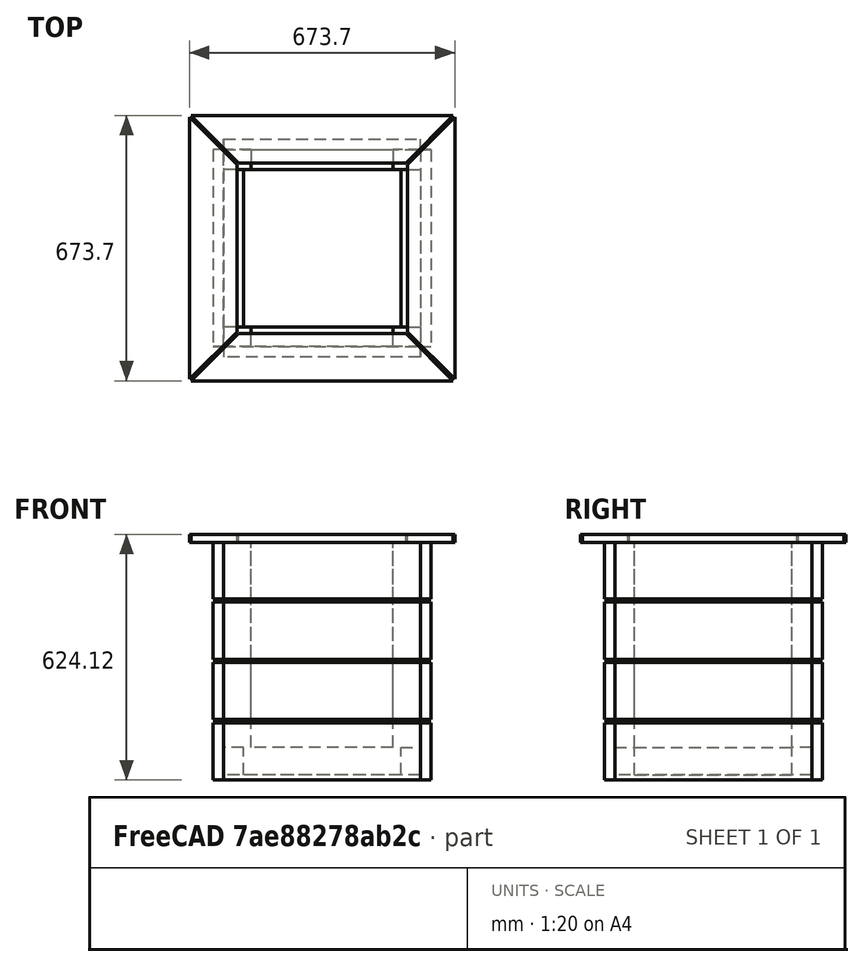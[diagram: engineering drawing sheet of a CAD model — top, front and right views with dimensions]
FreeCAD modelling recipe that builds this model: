
FCSTD DOCUMENT  (FreeCAD 0.18R16110 (Git))
Label: jardiniere
License: All rights reserved
LicenseURL: http://en.wikipedia.org/wiki/All_rights_reserved
objects: TechDraw::DrawViewDimension×11, TechDraw::DrawViewPart×6, Sketcher::SketchObject×4, PartDesign::Pad×4, PartDesign::Mirrored×4, TechDraw::DrawViewAnnotation×4, PartDesign::Plane×3, PartDesign::MultiTransform×3, PartDesign::PolarPattern×2, TechDraw::DrawViewSection×2, PartDesign::LinearPattern×1, PartDesign::Body×1, TechDraw::DrawSVGTemplate×1, TechDraw::DrawPage×1
note: 26 computed .brp shape members not serialized (recipe doc carries the construction recipe); baked Part::Feature solids carry a one-line shape summary decoded from their .brp

FEATURE [Sketcher::SketchObject] Sketch
  MapMode = 5
  Support = -> [XY_Plane]
  sketch-geometry (8):
    g0: LineSegment StartX=-250 StartY=250 StartZ=0 EndX=250 EndY=250 EndZ=0
    g1: LineSegment StartX=250 StartY=250 StartZ=0 EndX=250 EndY=-250 EndZ=0
    g2: LineSegment StartX=250 StartY=-250 StartZ=0 EndX=-250 EndY=-250 EndZ=0
    g3: LineSegment StartX=-250 StartY=-250 StartZ=0 EndX=-250 EndY=250 EndZ=0
    g4: LineSegment StartX=-200 StartY=200 StartZ=0 EndX=200 EndY=200 EndZ=0
    g5: LineSegment StartX=200 StartY=200 StartZ=0 EndX=200 EndY=-200 EndZ=0
    g6: LineSegment StartX=200 StartY=-200 StartZ=0 EndX=-200 EndY=-200 EndZ=0
    g7: LineSegment StartX=-200 StartY=-200 StartZ=0 EndX=-200 EndY=200 EndZ=0
  constraints (22):
    c: Coincident(g0,g1)
    c: Vertical(g1)
    c: Coincident(g1,g2)
    c: Horizontal(g2)
    c: Coincident(g2,g3)
    c: Coincident(g3,g0)
    c: DistanceX(g0,g0) = 500
    c: DistanceY(g3,g3) = 500
    c: Symmetric(g0,g2,g-1)
    c: Symmetric(g0,g0,g-2)
    c: Coincident(g4,g5)
    c: Coincident(g5,g6)
    c: Coincident(g6,g7)
    c: Coincident(g7,g4)
    c: Horizontal(g4)
    c: Horizontal(g6)
    c: Vertical(g5)
    c: Vertical(g7)
    c: DistanceX(g5,g1) = 50
    c: DistanceY(g1,g5) = 50
    c: DistanceY(g4,g0) = 50
    c: DistanceX(g0,g4) = 50
FEATURE [PartDesign::Pad] Pad
  Length = 70
  Length2 = 100
  Profile = -> Sketch
  Type = 0
FEATURE [PartDesign::Plane] DatumPlane
  Length = 808.439
  MapMode = 5
  Placement = pos=(0,0,70) rot=(0,0,1;0rad)
  ResizeMode = 0
  Support = -> [Pad]
  Width = 808.439
FEATURE [Sketcher::SketchObject] Sketch001
  ExternalGeometry = -> [Pad]
  MapMode = 5
  Placement = pos=(0,0,70) rot=(0,0,1;0rad)
  Support = -> [DatumPlane]
  sketch-geometry (4):
    g0: LineSegment StartX=-250 StartY=250 StartZ=0 EndX=-180 EndY=250 EndZ=0
    g1: LineSegment StartX=-180 StartY=250 StartZ=0 EndX=-180 EndY=200 EndZ=0
    g2: LineSegment StartX=-180 StartY=200 StartZ=0 EndX=-250 EndY=200 EndZ=0
    g3: LineSegment StartX=-250 StartY=200 StartZ=0 EndX=-250 EndY=250 EndZ=0
  constraints (11):
    c: Coincident(g0,g1)
    c: Coincident(g1,g2)
    c: Coincident(g2,g3)
    c: Coincident(g3,g0)
    c: Horizontal(g0)
    c: Horizontal(g2)
    c: Vertical(g1)
    c: Vertical(g3)
    c: Coincident(g0,g-4)
    c: PointOnObject(g1,g-6)
    c: DistanceX(g0,g0) = 70
FEATURE [PartDesign::Pad] Pad001
  BaseFeature = -> Pad
  Length = 520
  Length2 = 100
  Profile = -> Sketch001
  Type = 0
FEATURE [PartDesign::Mirrored] Mirrored
  MirrorPlane = -> Sketch001 [H_Axis]
FEATURE [PartDesign::Mirrored] Mirrored001
  MirrorPlane = -> Sketch001 [V_Axis]
FEATURE [PartDesign::MultiTransform] MultiTransform
  BaseFeature = -> Pad001
  Originals = -> [Pad001]
  Transformations = -> [Mirrored,Mirrored001]
FEATURE [PartDesign::Plane] DatumPlane001
  Length = 803.386
  MapMode = 5
  Placement = pos=(0,250,0) rot=(0,0.707107,0.707107;3.14159rad)
  ResizeMode = 0
  Support = -> [Pad001]
  Width = 753.809
FEATURE [Sketcher::SketchObject] Sketch002
  ExternalGeometry = -> [MultiTransform]
  MapMode = 5
  Placement = pos=(0,250,0) rot=(0,0.707107,0.707107;3.14159rad)
  Support = -> [DatumPlane001]
  sketch-geometry (4):
    g0: LineSegment StartX=-250 StartY=131.878 StartZ=0 EndX=250 EndY=131.878 EndZ=0
    g1: LineSegment StartX=250 StartY=131.878 StartZ=0 EndX=250 EndY=-13.1218 EndZ=0
    g2: LineSegment StartX=250 StartY=-13.1218 StartZ=0 EndX=-250 EndY=-13.1218 EndZ=0
    g3: LineSegment StartX=-250 StartY=-13.1218 StartZ=0 EndX=-250 EndY=131.878 EndZ=0
  constraints (11):
    c: Coincident(g0,g1)
    c: Coincident(g1,g2)
    c: Coincident(g2,g3)
    c: Coincident(g3,g0)
    c: Horizontal(g0)
    c: Horizontal(g2)
    c: Vertical(g1)
    c: Vertical(g3)
    c: PointOnObject(g1,g-4)
    c: DistanceY(g3,g3) = 145
    c: PointOnObject(g0,g-3)
FEATURE [PartDesign::Pad] Pad002
  BaseFeature = -> MultiTransform
  Length = 27
  Length2 = 100
  Profile = -> Sketch002
  Type = 0
FEATURE [PartDesign::LinearPattern] LinearPattern
  Direction = -> Sketch002 [V_Axis]
  Length = 460
  Occurrences = 4
FEATURE [PartDesign::Mirrored] Mirrored002
  MirrorPlane = -> XZ_Plane
FEATURE [PartDesign::PolarPattern] PolarPattern
  Angle = 90
  Axis = -> Z_Axis
  Occurrences = 2
FEATURE [PartDesign::MultiTransform] MultiTransform001
  BaseFeature = -> Pad002
  Originals = -> [Pad002]
  Transformations = -> [LinearPattern,Mirrored002,PolarPattern]
FEATURE [PartDesign::Plane] DatumPlane002
  Length = 808.439
  MapMode = 5
  Placement = pos=(0,0,590) rot=(0,0,1;0rad)
  ResizeMode = 0
  Support = -> [MultiTransform001]
  Width = 808.439
FEATURE [Sketcher::SketchObject] Sketch003
  MapMode = 5
  Placement = pos=(0,0,590) rot=(0,0,1;0rad)
  Support = -> [DatumPlane002]
  sketch-geometry (4):
    g0: LineSegment StartX=-332.5 StartY=336.85 StartZ=0 EndX=332.5 EndY=336.85 EndZ=0
    g1: LineSegment StartX=332.5 StartY=336.85 StartZ=0 EndX=212.5 EndY=216.85 EndZ=0
    g2: LineSegment StartX=212.5 StartY=216.85 StartZ=0 EndX=-212.5 EndY=216.85 EndZ=0
    g3: LineSegment StartX=-212.5 StartY=216.85 StartZ=0 EndX=-332.5 EndY=336.85 EndZ=0
  constraints (10):
    c: Coincident(g0,g1)
    c: Coincident(g1,g2)
    c: Coincident(g2,g3)
    c: Coincident(g3,g0)
    c: Angle(g3,g0) = 0.785398
    c: Angle(g0,g1) = 0.785398
    c: DistanceX(g2,g2) = 425
    c: DistanceY(g1,g0) = 120
    c: DistanceX(g0,g0) = 665
    c: Symmetric(g2,g1,g-2)
FEATURE [PartDesign::Pad] Pad003
  BaseFeature = -> MultiTransform001
  Length = 21
  Length2 = 100
  Profile = -> Sketch003
  Type = 0
FEATURE [PartDesign::Mirrored] Mirrored003
  MirrorPlane = -> Sketch003 [H_Axis]
FEATURE [PartDesign::PolarPattern] PolarPattern001
  Angle = 90
  Axis = -> Sketch003 [N_Axis]
  Occurrences = 2
FEATURE [PartDesign::MultiTransform] MultiTransform002
  BaseFeature = -> Pad003
  Originals = -> [Pad003]
  Transformations = -> [Mirrored003,PolarPattern001]
FEATURE [PartDesign::Body] Body
  Group = -> [Sketch,Pad,DatumPlane,Sketch001,Pad001,MultiTransform,Mirrored,Mirrored001,DatumPlane001,Sketch002,Pad002,MultiTransform001,LinearPattern,Mirrored002,PolarPattern,DatumPlane002,Sketch003,Pad003,MultiTransform002,Mirrored003,PolarPattern001]
  Origin = -> Origin
  Tip = -> MultiTransform002
FEATURE [TechDraw::DrawSVGTemplate] Template
  EditableTexts = Designed_by_Name=Y. Labrit; Drawing_number=Drawing number; FC-Date=01/07/2018; FC-SC=Scale; FC-SH=Sheet; FC-Title=Jardiniere cube; Subtitle=Subtitle; Weight=Weight
  Height = 210
  Orientation = 1
  Width = 297
FEATURE [TechDraw::DrawViewPart] View
  CoarseView = false
  Direction = (0,1,0)
  Focus = 100
  HardHidden = false
  IsoCount = 0
  IsoHidden = false
  IsoVisible = false
  LockPosition = false
  Perspective = false
  Rotation = 0
  Scale = 0.07
  ScaleType = 2
  SeamHidden = false
  SeamVisible = false
  SmoothHidden = false
  SmoothVisible = false
  Source = -> [MultiTransform002]
  X = 58.3303
  Y = 105.073
FEATURE [TechDraw::DrawViewSection] Section  label="Section A - A"
  BaseView = -> View
  CoarseView = false
  Direction = (0,0,1)
  Focus = 100
  FuseBeforeCut = true
  HardHidden = false
  HatchScale = 1
  IsoCount = 0
  IsoHidden = false
  IsoVisible = false
  LockPosition = false
  NameGeomPattern = Diamond
  Perspective = false
  Rotation = 0
  Scale = 0.07
  ScaleType = 2
  SeamHidden = false
  SeamVisible = false
  SectionDirection = 3
  SectionNormal = (0,0,1)
  SectionOrigin = (0,0,298.939)
  SectionSymbol = A
  SmoothHidden = false
  SmoothVisible = false
  Source = -> [MultiTransform002]
  X = 57.2775
  Y = 45.8237
FEATURE [TechDraw::DrawViewSection] Section001  label="Section A - A001"
  BaseView = -> View
  CoarseView = false
  Direction = (1,0,0)
  Focus = 100
  FuseBeforeCut = true
  HardHidden = false
  HatchScale = 1
  IsoCount = 0
  IsoHidden = false
  IsoVisible = false
  LockPosition = false
  NameGeomPattern = Diamond
  Perspective = false
  Rotation = 0
  Scale = 0.07
  ScaleType = 2
  SeamHidden = false
  SeamVisible = false
  SectionDirection = 0
  SectionNormal = (1,0,0)
  SectionOrigin = (0,0,298.94)
  SectionSymbol = A
  SmoothHidden = false
  SmoothVisible = false
  Source = -> [MultiTransform002]
  X = 120.156
  Y = 104.575
FEATURE [TechDraw::DrawViewPart] View001
  CoarseView = false
  Direction = (0,0,1)
  Focus = 100
  HardHidden = false
  IsoCount = 0
  IsoHidden = false
  IsoVisible = false
  LockPosition = false
  Perspective = false
  Rotation = 0
  Scale = 0.05
  ScaleType = 2
  SeamHidden = false
  SeamVisible = false
  SmoothHidden = false
  SmoothVisible = false
  Source = -> [MultiTransform002]
  X = 57.2911
  Y = 163.823
FEATURE [TechDraw::DrawViewDimension] Dimension014
  Arbitrary = false
  FormatSpec = %.2f
  LockPosition = false
  MeasureType = 1
  OverTolerance = 0
  References2D = -> [Section]
  Rotation = 0
  ScaleType = 0
  Type = 2
  UnderTolerance = 0
  X = 28.896
  Y = -1.49114
FEATURE [TechDraw::DrawViewDimension] Dimension015
  Arbitrary = false
  FormatSpec = %.2f
  LockPosition = false
  MeasureType = 1
  OverTolerance = 0
  References2D = -> [Section]
  Rotation = 0
  ScaleType = 0
  Type = 1
  UnderTolerance = 0
  X = 0
  Y = -27.0321
FEATURE [TechDraw::DrawViewDimension] Dimension016
  Arbitrary = false
  FormatSpec = %.2f
  LockPosition = false
  MeasureType = 1
  OverTolerance = 0
  References2D = -> [Section001]
  Rotation = 0
  ScaleType = 0
  Type = 2
  UnderTolerance = 0
  X = 27.7953
  Y = -6.48469
FEATURE [TechDraw::DrawViewDimension] Dimension017
  Arbitrary = false
  FormatSpec = %.2f
  LockPosition = false
  MeasureType = 1
  OverTolerance = 0
  References2D = -> [Section001]
  Rotation = 0
  ScaleType = 0
  Type = 1
  UnderTolerance = 0
  X = 35.1592
  Y = -28.482
FEATURE [TechDraw::DrawViewDimension] Dimension018
  Arbitrary = false
  FormatSpec = %.2f
  LockPosition = false
  MeasureType = 1
  OverTolerance = 0
  References2D = -> [Section]
  Rotation = 0
  ScaleType = 0
  Type = 1
  UnderTolerance = 0
  X = 33.9777
  Y = 25.111
FEATURE [TechDraw::DrawViewAnnotation] Annotation
  Font = Times New Roman
  LineSpace = 80
  LockPosition = false
  MaxWidth = -1
  Rotation = 0
  ScaleType = 0
  Text = Base: 50x7x5 (2) / 40x7x5 (2) | Montants: 52x7x5 (4) | Cotes: 50x14,5x2,7 (16) | Cache: 66,5x12x2,1 (4)
  TextSize = 4
  TextStyle = 0
  X = 245.002
  Y = 105.167
FEATURE [TechDraw::DrawViewAnnotation] Annotation001
  Font = Times New Roman
  LineSpace = 80
  LockPosition = false
  MaxWidth = -1
  Rotation = 0
  ScaleType = 0
  Text = Base: 5x130mn (4) | Montants: 5x30 mn (4) | Cotes: 5x50 mn (72) | Cache: 5x50mn (8)
  TextSize = 4
  TextStyle = 0
  X = 235.051
  Y = 71.1326
FEATURE [TechDraw::DrawViewAnnotation] Annotation002
  Font = osifont
  LineSpace = 80
  LockPosition = false
  MaxWidth = -1
  Rotation = 0
  ScaleType = 0
  Text = Bois
  TextSize = 8
  TextStyle = 0
  X = 186.215
  Y = 111.17
FEATURE [TechDraw::DrawViewAnnotation] Annotation003
  Font = osifont
  LineSpace = 80
  LockPosition = false
  MaxWidth = -1
  Rotation = 0
  ScaleType = 0
  Text = Vis
  TextSize = 8
  TextStyle = 0
  X = 185.647
  Y = 76.7275
FEATURE [TechDraw::DrawViewDimension] Dimension027
  Arbitrary = false
  FormatSpec = %.2f
  LockPosition = false
  MeasureType = 1
  OverTolerance = 0
  References2D = -> [View001]
  Rotation = 0
  ScaleType = 0
  Type = 2
  UnderTolerance = 0
  X = -33.598
  Y = 0.492339
FEATURE [TechDraw::DrawViewPart] View004
  CoarseView = false
  Direction = (0.727,0.308,0.614)
  Focus = 100
  HardHidden = false
  IsoCount = 0
  IsoHidden = false
  IsoVisible = false
  LockPosition = false
  Perspective = false
  Rotation = 0
  Scale = 0.05
  ScaleType = 2
  SeamHidden = false
  SeamVisible = false
  SmoothHidden = false
  SmoothVisible = false
  Source = -> [MultiTransform002]
  X = 262.302
  Y = 170.37
FEATURE [TechDraw::DrawViewPart] View005
  CoarseView = false
  Direction = (0.727,0.308,0.614)
  Focus = 100
  HardHidden = false
  IsoCount = 0
  IsoHidden = false
  IsoVisible = false
  LockPosition = false
  Perspective = false
  Rotation = 0
  Scale = 0.05
  ScaleType = 2
  SeamHidden = false
  SeamVisible = false
  SmoothHidden = false
  SmoothVisible = false
  Source = -> [Pad002]
  X = 179.303
  Y = 167.734
FEATURE [TechDraw::DrawViewPart] View006
  CoarseView = false
  Direction = (0.727,0.308,0.614)
  Focus = 100
  HardHidden = false
  IsoCount = 0
  IsoHidden = false
  IsoVisible = false
  LockPosition = false
  Perspective = false
  Rotation = 0
  Scale = 0.05
  ScaleType = 2
  SeamHidden = false
  SeamVisible = false
  SmoothHidden = false
  SmoothVisible = false
  Source = -> [Pad003,MultiTransform001]
  X = 219.681
  Y = 169.095
FEATURE [TechDraw::DrawViewPart] View007
  CoarseView = false
  Direction = (0.727,0.308,0.614)
  Focus = 100
  HardHidden = false
  IsoCount = 0
  IsoHidden = false
  IsoVisible = false
  LockPosition = false
  Perspective = false
  Rotation = 0
  Scale = 0.05
  ScaleType = 2
  SeamHidden = false
  SeamVisible = false
  SmoothHidden = false
  SmoothVisible = false
  Source = -> [Pad]
  X = 142.38
  Y = 157.178
FEATURE [TechDraw::DrawViewDimension] Dimension
  Arbitrary = false
  FormatSpec = %.2f
  LockPosition = false
  MeasureType = 1
  OverTolerance = 0
  References2D = -> [View001]
  Rotation = 0
  ScaleType = 0
  Type = 2
  UnderTolerance = 0
  X = 23.3662
  Y = -1.49114
FEATURE [TechDraw::DrawViewDimension] Dimension028
  Arbitrary = false
  FormatSpec = %.2f
  LockPosition = false
  MeasureType = 1
  OverTolerance = 0
  References2D = -> [View001]
  Rotation = 0
  ScaleType = 0
  Type = 6
  UnderTolerance = 0
  X = -0.745569
  Y = 9.50601
FEATURE [TechDraw::DrawViewDimension] Dimension029
  Arbitrary = false
  FormatSpec = %.2f
  LockPosition = false
  MeasureType = 1
  OverTolerance = 0
  References2D = -> [Section001]
  Rotation = 0
  ScaleType = 0
  Type = 2
  UnderTolerance = 0
  X = 36.512
  Y = -2.29915
FEATURE [TechDraw::DrawViewDimension] Dimension030
  Arbitrary = false
  FormatSpec = %.2f
  LockPosition = false
  MeasureType = 1
  OverTolerance = 0
  References2D = -> [Section001]
  Rotation = 0
  ScaleType = 0
  Type = 2
  UnderTolerance = 0
  X = 27.6801
  Y = 19.9909
FEATURE [TechDraw::DrawViewDimension] Dimension031
  Arbitrary = false
  FormatSpec = %.2f
  LockPosition = false
  MeasureType = 1
  OverTolerance = 0
  References2D = -> [View]
  Rotation = 0
  ScaleType = 0
  Type = 2
  UnderTolerance = 0
  X = -43.2221
  Y = 13.3489
FEATURE [TechDraw::DrawPage] Page
  KeepUpdated = true
  ProjectionType = 0
  Template = -> Template
  Views = -> [View,Section,Section001,View001,Dimension014,Dimension015,Dimension016,Dimension017,Dimension018,Annotation,Annotation001,Annotation002,Annotation003,Dimension027,View004,View005,View006,View007,Dimension,Dimension028,Dimension029,Dimension030,Dimension031]
